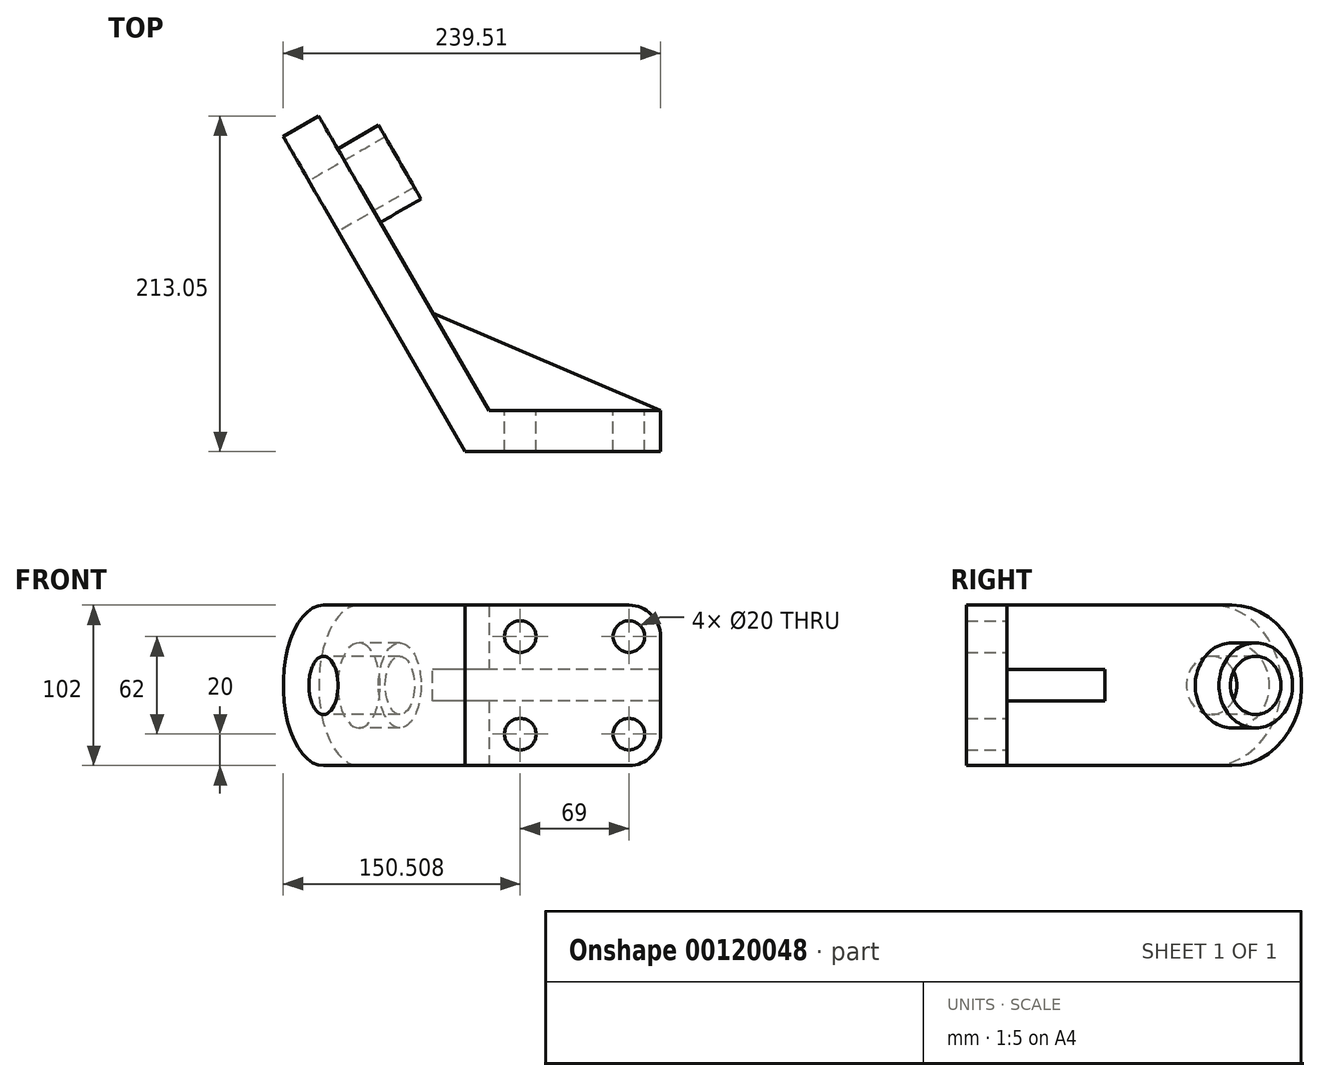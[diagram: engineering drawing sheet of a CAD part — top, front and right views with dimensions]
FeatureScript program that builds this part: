
annotation { "Feature Type Name" : "Feature", "Feature Type Description" : "" }
export const myFeature = defineFeature(function(context is Context, id is Id, definition is map)
    precondition{}
    {
        {
            var Q0;
            Q0=qCreatedBy(makeId("Top.planeOp"),FACE);
            var sketch = newSketch(context, id + "F0", { "sketchPlane" : qUnion([Q0])});
            skLineSegment(sketch, "E0", {"start": v(-111.52, 92.14) * mm, "end": v(-134.03, 79.14) * mm});
            skLineSegment(sketch, "E1", {"start": v(-134.03, 79.14) * mm, "end": v(-18.53, -120.91) * mm});
            skLineSegment(sketch, "E2", {"start": v(-18.53, -120.91) * mm, "end": v(105.48, -120.91) * mm});
            skLineSegment(sketch, "E3", {"start": v(105.48, -120.91) * mm, "end": v(105.48, -94.91) * mm});
            skLineSegment(sketch, "E4", {"start": v(105.48, -94.91) * mm, "end": v(-3.52, -94.91) * mm});
            skLineSegment(sketch, "E5", {"start": v(-3.52, -94.91) * mm, "end": v(-111.52, 92.14) * mm});
            skSolve(sketch);
        }
        {
            var Q0;
            Q0=makeQuery(id+"F0.imprint","IMPRINT",FACE,{"disambiguationData":[TD([[makeQuery(id+"F0.imprint","IMPRINT",EDGE,{"derivedFrom":sQuery(id+"F0.wireOp",EDGE,"E0")}),1.0]])]});
            extrude(context, id + "F1", {"entities" : qUnion([Q0]), "depth" : 102 * mm});
        }
        {
            var Q0;
            Q0=makeQuery(id+"F1.opExtrude","CAP_EDGE",EDGE,{"disambiguationData":[OSD([sQuery(id+"F0.wireOp",EDGE,"E0")])],"isStart":false});
            var Q1;
            Q1=makeQuery(id+"F1.opExtrude","CAP_EDGE",EDGE,{"disambiguationData":[OSD([sQuery(id+"F0.wireOp",EDGE,"E0")])],"isStart":true});
            fillet(context, id + "F2", {"entities" : qUnion([Q0, Q1]), "radius" : 51 * mm, "tangentPropagation" : true, "allowEdgeOverflow" : false});
        }
        {
            var Q0;
            Q0=makeQuery(id+"F1.opExtrude","SWEPT_FACE",FACE,{"disambiguationData":[OSD([sQuery(id+"F0.wireOp",EDGE,"E5")])]});
            var sketch = newSketch(context, id + "F3", { "sketchPlane" : qUnion([Q0])});
            skCircle(sketch, "E6", {"center": v(84.55, 51) * mm, "radius": 27 * mm});
            skCircle(sketch, "E7", {"center": v(84.55, 51) * mm, "radius": 18.5 * mm});
            skSolve(sketch);
        }
        {
            var Q0;
            Q0 = qSketchRegion(id + "F3", true);
            extrude(context, id + "F4", {"entities" : qUnion([Q0]), "operationType" : NewBodyOperationType.ADD, "depth" : 30 * mm});
        }
        {
            var Q0;
            Q0=makeQuery(id+"F1.opExtrude","SWEPT_FACE",FACE,{"disambiguationData":[OSD([sQuery(id+"F0.wireOp",EDGE,"E4")])]});
            var sketch = newSketch(context, id + "F5", { "sketchPlane" : qUnion([Q0])});
            skCircle(sketch, "E8", {"center": v(-85.48, 82) * mm, "radius": 10 * mm});
            skCircle(sketch, "E9.0.1.0", {"center": v(-85.48, 20) * mm, "radius": 10 * mm});
            skCircle(sketch, "E9.1.0.0", {"center": v(-16.48, 82) * mm, "radius": 10 * mm});
            skCircle(sketch, "E9.1.1.0", {"center": v(-16.48, 20) * mm, "radius": 10 * mm});
            skLineSegment(sketch, "E9.direction1", {"start": v(-85.48, 82) * mm, "end": v(-16.48, 82) * mm, "construction": true});
            skLineSegment(sketch, "E9.direction2", {"start": v(-85.48, 82) * mm, "end": v(-85.48, 20) * mm, "construction": true});
            skSolve(sketch);
        }
        {
            var Q0;
            Q0=makeQuery(id+"F1.opExtrude","CAP_FACE",FACE,{"disambiguationData":[OSD([sQuery(id+"F0.wireOp",EDGE,"E0"),sQuery(id+"F0.wireOp",EDGE,"E1"),sQuery(id+"F0.wireOp",EDGE,"E2"),sQuery(id+"F0.wireOp",EDGE,"E3"),sQuery(id+"F0.wireOp",EDGE,"E4"),sQuery(id+"F0.wireOp",EDGE,"E5")])],"isStart":false});
            cPlane(context, id + "F6", {"entities" : qUnion([Q0]), "cplaneType" : CPlaneType.OFFSET, "offset" : 51 * mm, "oppositeDirection" : true, "width" : 150 * mm, "height" : 150 * mm});
        }
        {
            var Q0;
            Q0=qCreatedBy(id+"F6.planeOp",FACE);
            var sketch = newSketch(context, id + "F7", { "sketchPlane" : qUnion([Q0])});
            skLineSegment(sketch, "E10.0", {"start": v(105.48, -94.91) * mm, "end": v(-3.52, -94.91) * mm});
            skLineSegment(sketch, "E11", {"start": v(105.48, -94.91) * mm, "end": v(-44.26, -30.75) * mm});
            skLineSegment(sketch, "E12", {"start": v(-44.26, -30.75) * mm, "end": v(-3.52, -94.91) * mm});
            skSolve(sketch);
        }
        {
            var Q0;
            Q0 = qSketchRegion(id + "F7", true);
            extrude(context, id + "F8", {"entities" : qUnion([Q0]), "operationType" : NewBodyOperationType.ADD, "endBound" : BoundingType.SYMMETRIC, "depth" : 20 * mm});
        }
        {
            var Q0;
            Q0 = qSketchRegion(id + "F5", true);
            extrude(context, id + "F9", {"entities" : qUnion([Q0]), "operationType" : NewBodyOperationType.REMOVE, "oppositeDirection" : true, "depth" : 30 * mm});
        }
        {
            var Q0;
            {var subQ1=sQuery(id+"F0.wireOp",EDGE,"E4");var subQ2=sQuery(id+"F0.wireOp",EDGE,"E5");Q0=makeQuery(id+"F4.boolean.opBoolean","SPLIT",FACE,{"disambiguationData":[TD([makeQuery(id+"F1.opExtrude","SWEPT_FACE",FACE,{"disambiguationData":[OSD([subQ1])]})])],"derivedFrom":makeQuery(id+"F1.opExtrude","SWEPT_FACE",FACE,{"disambiguationData":[OSD([subQ2])]})});}
            var sketch = newSketch(context, id + "F10", { "sketchPlane" : qUnion([Q0])});
            skCircle(sketch, "E13.0", {"center": v(84.55, 51) * mm, "radius": 18.5 * mm});
            skSolve(sketch);
        }
        {
            var Q0;
            Q0=makeQuery(id+"F10.imprint","IMPRINT",FACE,{"disambiguationData":[TD([[makeQuery(id+"F10.imprint","IMPRINT",EDGE,{"derivedFrom":sQuery(id+"F10.wireOp",EDGE,"E13.0")}),1.0]])]});
            extrude(context, id + "F11", {"entities" : qUnion([Q0]), "operationType" : NewBodyOperationType.REMOVE, "oppositeDirection" : true, "depth" : 30 * mm});
        }
        {
            var Q0;
            Q0=makeQuery(id+"F1.opExtrude","CAP_EDGE",EDGE,{"disambiguationData":[OSD([sQuery(id+"F0.wireOp",EDGE,"E3")])],"isStart":false});
            fillet(context, id + "F12", {"entities" : qUnion([Q0]), "radius" : 20 * mm, "tangentPropagation" : true, "allowEdgeOverflow" : false});
        }
        {
            var Q0;
            Q0=makeQuery(id+"F1.opExtrude","CAP_EDGE",EDGE,{"disambiguationData":[OSD([sQuery(id+"F0.wireOp",EDGE,"E3")])],"isStart":true});
            fillet(context, id + "F13", {"entities" : qUnion([Q0]), "radius" : 20 * mm, "tangentPropagation" : true, "allowEdgeOverflow" : false});
        }
    });
